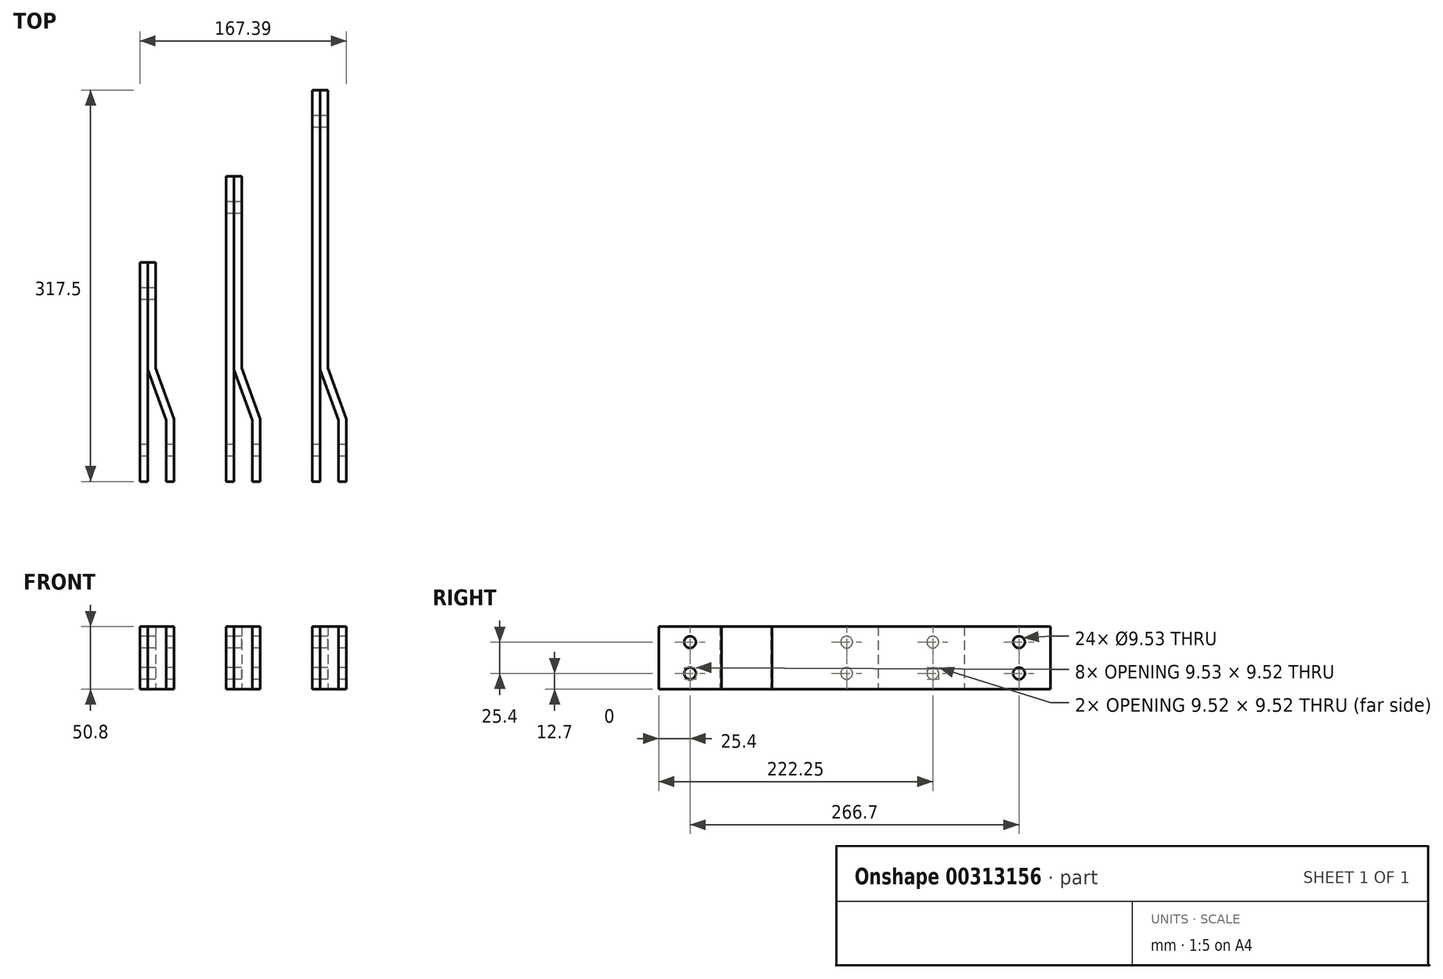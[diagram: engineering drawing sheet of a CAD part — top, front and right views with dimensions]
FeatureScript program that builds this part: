
annotation { "Feature Type Name" : "Feature", "Feature Type Description" : "" }
export const myFeature = defineFeature(function(context is Context, id is Id, definition is map)
    precondition{}
    {
        {
            var Q0;
            Q0=qCreatedBy(makeId("Top.planeOp"),FACE);
            var sketch = newSketch(context, id + "F0", { "sketchPlane" : qUnion([Q0])});
            skLineSegment(sketch, "E0.bottom", {"start": v(0, 177.8) * mm, "end": v(6.35, 177.8) * mm});
            skLineSegment(sketch, "E0.top", {"start": v(0, 0) * mm, "end": v(6.35, 0) * mm});
            skLineSegment(sketch, "E0.left", {"start": v(0, 177.8) * mm, "end": v(0, 0) * mm});
            skLineSegment(sketch, "E0.right", {"start": v(6.35, 177.8) * mm, "end": v(6.35, 0) * mm});
            skLineSegment(sketch, "E1.bottom", {"start": v(69.85, 247.65) * mm, "end": v(76.2, 247.65) * mm});
            skLineSegment(sketch, "E1.top", {"start": v(69.85, 0) * mm, "end": v(76.2, 0) * mm});
            skLineSegment(sketch, "E1.left", {"start": v(69.85, 247.65) * mm, "end": v(69.85, 0) * mm});
            skLineSegment(sketch, "E1.right", {"start": v(76.2, 247.65) * mm, "end": v(76.2, 0) * mm});
            skLineSegment(sketch, "E2.bottom", {"start": v(139.7, 317.5) * mm, "end": v(146.05, 317.5) * mm});
            skLineSegment(sketch, "E2.top", {"start": v(139.7, 0) * mm, "end": v(146.05, 0) * mm});
            skLineSegment(sketch, "E2.left", {"start": v(139.7, 317.5) * mm, "end": v(139.7, 0) * mm});
            skLineSegment(sketch, "E2.right", {"start": v(146.05, 317.5) * mm, "end": v(146.05, 0) * mm});
            skSolve(sketch);
        }
        {
            var Q0;
            Q0=qSketchRegion(id+"F0",true);
            extrude(context, id + "F1", {"entities" : qUnion([Q0]), "endBound" : BoundingType.SYMMETRIC, "depth" : 50.8 * mm});
        }
        {
            var Q0;
            Q0=qCreatedBy(makeId("Top.planeOp"),FACE);
            var sketch = newSketch(context, id + "F2", { "sketchPlane" : qUnion([Q0])});
            skLineSegment(sketch, "E3", {"start": v(21.34, 0) * mm, "end": v(27.69, 0) * mm});
            skLineSegment(sketch, "E4", {"start": v(27.69, 0) * mm, "end": v(27.69, 50.8) * mm});
            skLineSegment(sketch, "E5", {"start": v(27.69, 50.8) * mm, "end": v(12.7, 91.97) * mm});
            skLineSegment(sketch, "E6", {"start": v(12.7, 91.97) * mm, "end": v(12.7, 177.8) * mm});
            skLineSegment(sketch, "E7", {"start": v(12.7, 177.8) * mm, "end": v(6.35, 177.8) * mm});
            skLineSegment(sketch, "E8", {"start": v(6.35, 177.8) * mm, "end": v(6.35, 90.85) * mm});
            skLineSegment(sketch, "E9", {"start": v(6.35, 90.85) * mm, "end": v(21.34, 49.68) * mm});
            skLineSegment(sketch, "E10", {"start": v(21.34, 49.68) * mm, "end": v(21.34, 0) * mm});
            skLineSegment(sketch, "E11", {"start": v(91.19, 0) * mm, "end": v(97.54, 0) * mm});
            skLineSegment(sketch, "E12", {"start": v(97.54, 0) * mm, "end": v(97.54, 50.8) * mm});
            skLineSegment(sketch, "E13", {"start": v(97.54, 50.8) * mm, "end": v(82.55, 91.97) * mm});
            skLineSegment(sketch, "E14", {"start": v(76.2, 90.85) * mm, "end": v(91.19, 49.68) * mm});
            skLineSegment(sketch, "E15", {"start": v(91.19, 49.68) * mm, "end": v(91.19, 0) * mm});
            skLineSegment(sketch, "E16", {"start": v(161.04, 0) * mm, "end": v(167.39, 0) * mm});
            skLineSegment(sketch, "E17", {"start": v(167.39, 0) * mm, "end": v(167.39, 50.8) * mm});
            skLineSegment(sketch, "E18", {"start": v(167.39, 50.8) * mm, "end": v(152.4, 91.97) * mm});
            skLineSegment(sketch, "E19", {"start": v(146.05, 90.85) * mm, "end": v(161.04, 49.68) * mm});
            skLineSegment(sketch, "E20", {"start": v(161.04, 49.68) * mm, "end": v(161.04, 0) * mm});
            skLineSegment(sketch, "E21", {"start": v(76.2, 90.85) * mm, "end": v(76.2, 247.65) * mm});
            skLineSegment(sketch, "E22", {"start": v(76.2, 247.65) * mm, "end": v(82.55, 247.65) * mm});
            skLineSegment(sketch, "E23", {"start": v(82.55, 247.65) * mm, "end": v(82.55, 91.97) * mm});
            skLineSegment(sketch, "E24", {"start": v(146.05, 90.85) * mm, "end": v(146.05, 317.5) * mm});
            skLineSegment(sketch, "E25", {"start": v(146.05, 317.5) * mm, "end": v(152.4, 317.5) * mm});
            skLineSegment(sketch, "E26", {"start": v(152.4, 317.5) * mm, "end": v(152.4, 91.97) * mm});
            skSolve(sketch);
        }
        {
            var Q0;
            Q0=qSketchRegion(id+"F2",true);
            extrude(context, id + "F3", {"entities" : qUnion([Q0]), "endBound" : BoundingType.SYMMETRIC, "depth" : 50.8 * mm});
        }
        {
            var Q0;
            Q0=makeQuery(id+"F1.opExtrude","SWEPT_FACE",FACE,{"disambiguationData":[OSD([sQuery(id+"F0.wireOp",EDGE,"E0.left")])]});
            var sketch = newSketch(context, id + "F4", { "sketchPlane" : qUnion([Q0])});
            skCircle(sketch, "E27", {"center": v(-25.4, 12.7) * mm, "radius": 4.76 * mm});
            skCircle(sketch, "E28", {"center": v(-25.4, -12.7) * mm, "radius": 4.76 * mm});
            skLineSegment(sketch, "E29", {"start": v(-25.4, 12.7) * mm, "end": v(-25.4, -12.7) * mm, "construction": true});
            skPoint(sketch, "E30", {"position": v(-25.4, 0) * mm});
            skSolve(sketch);
        }
        {
            var Q0;
            Q0=qSketchRegion(id+"F4",true);
            extrude(context, id + "F5", {"entities" : qUnion([Q0]), "operationType" : NewBodyOperationType.REMOVE, "endBound" : BoundingType.THROUGH_ALL, "oppositeDirection" : true, "depth" : 25.4 * mm});
        }
        {
            var Q0;
            Q0=makeQuery(id+"F1.opExtrude","SWEPT_FACE",FACE,{"disambiguationData":[OSD([sQuery(id+"F0.wireOp",EDGE,"E0.left")])]});
            var sketch = newSketch(context, id + "F6", { "sketchPlane" : qUnion([Q0])});
            skCircle(sketch, "E31", {"center": v(-152.4, 12.7) * mm, "radius": 4.76 * mm});
            skCircle(sketch, "E32", {"center": v(-152.4, -12.7) * mm, "radius": 4.76 * mm});
            skLineSegment(sketch, "E33", {"start": v(-152.4, 12.7) * mm, "end": v(-152.4, -12.7) * mm, "construction": true});
            skPoint(sketch, "E34", {"position": v(-152.4, 0) * mm});
            skSolve(sketch);
        }
        {
            var Q0;
            Q0=qSketchRegion(id+"F6",true);
            var Q1;
            Q1=makeQuery(id+"F3.opExtrude","SWEPT_FACE",FACE,{"disambiguationData":[OSD([sQuery(id+"F2.wireOp",EDGE,"E6")])]});
            extrude(context, id + "F7", {"entities" : qUnion([Q0]), "operationType" : NewBodyOperationType.REMOVE, "endBound" : BoundingType.UP_TO_SURFACE, "oppositeDirection" : true, "endBoundEntityFace" : qUnion([Q1]), "depth" : 25.4 * mm});
        }
        {
            var Q0;
            Q0=makeQuery(id+"F1.opExtrude","SWEPT_FACE",FACE,{"disambiguationData":[OSD([sQuery(id+"F0.wireOp",EDGE,"E1.left")])]});
            var sketch = newSketch(context, id + "F8", { "sketchPlane" : qUnion([Q0])});
            skCircle(sketch, "E35", {"center": v(-222.25, 12.7) * mm, "radius": 4.76 * mm});
            skCircle(sketch, "E36", {"center": v(-222.25, -12.7) * mm, "radius": 4.76 * mm});
            skLineSegment(sketch, "E37", {"start": v(-222.25, 12.7) * mm, "end": v(-222.25, -12.7) * mm, "construction": true});
            skPoint(sketch, "E38", {"position": v(-222.25, 0) * mm});
            skSolve(sketch);
        }
        {
            var Q0;
            Q0=qSketchRegion(id+"F8",true);
            var Q1;
            Q1=makeQuery(id+"F3.opExtrude","SWEPT_FACE",FACE,{"disambiguationData":[OSD([sQuery(id+"F2.wireOp",EDGE,"E23")])]});
            extrude(context, id + "F9", {"entities" : qUnion([Q0]), "operationType" : NewBodyOperationType.REMOVE, "endBound" : BoundingType.UP_TO_SURFACE, "oppositeDirection" : true, "endBoundEntityFace" : qUnion([Q1]), "depth" : 25.4 * mm});
        }
        {
            var Q0;
            Q0=makeQuery(id+"F1.opExtrude","SWEPT_FACE",FACE,{"disambiguationData":[OSD([sQuery(id+"F0.wireOp",EDGE,"E2.left")])]});
            var sketch = newSketch(context, id + "F10", { "sketchPlane" : qUnion([Q0])});
            skCircle(sketch, "E39", {"center": v(-292.1, 12.7) * mm, "radius": 4.76 * mm});
            skCircle(sketch, "E40", {"center": v(-292.1, -12.7) * mm, "radius": 4.76 * mm});
            skLineSegment(sketch, "E41", {"start": v(-292.1, 12.7) * mm, "end": v(-292.1, -12.7) * mm, "construction": true});
            skPoint(sketch, "E42", {"position": v(-292.1, 0) * mm});
            skSolve(sketch);
        }
        {
            var Q0;
            Q0=qSketchRegion(id+"F10",true);
            var Q1;
            Q1=makeQuery(id+"F3.opExtrude","SWEPT_FACE",FACE,{"disambiguationData":[OSD([sQuery(id+"F2.wireOp",EDGE,"E26")])]});
            extrude(context, id + "F11", {"entities" : qUnion([Q0]), "operationType" : NewBodyOperationType.REMOVE, "endBound" : BoundingType.UP_TO_SURFACE, "oppositeDirection" : true, "endBoundEntityFace" : qUnion([Q1]), "depth" : 25.4 * mm});
        }
    });
